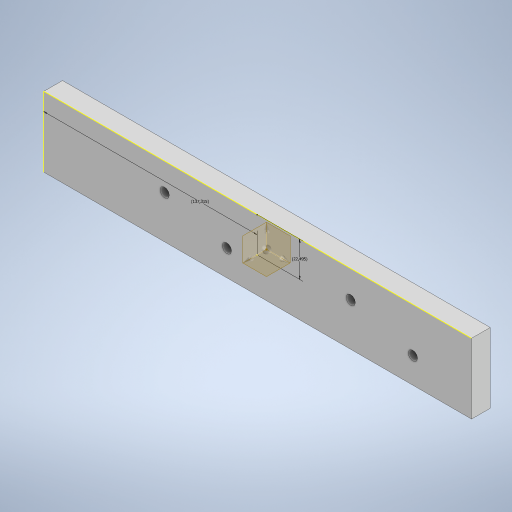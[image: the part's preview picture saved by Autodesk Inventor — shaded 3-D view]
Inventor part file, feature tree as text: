
AUTODESK INVENTOR PART (.ipt)
format: ipt  version: 2024 (Build 280153000, 153)  size: 239,616 bytes
history: native  units: mm
features: other x6, sketch x1
ambient origin geometry x8: Origin, YZ Plane, XZ Plane, XY Plane, X Axis, Y Axis, Z Axis, Center Point
bodies: Body1 (feature_tree)
feature tree (7):
  other  "BORDE_3"
  other  "Generador_de_Piezas.ipt"
  other  "Desplazar cuerpo1"
  sketch  "Boceto1"  dims[d0=10.0mm d1=-180.582mm d2=-2338.516mm d3=0.0mm d4=22.49535mm d5=137.315464mm d6=0.185mm d7=-0.005mm d8=0.0mm]
  other  "Desplazar cuerpo2"
  other  "BORDE_3::Generador_de_Piezas.ipt"
  other  "OperaciónIdentificador1"
